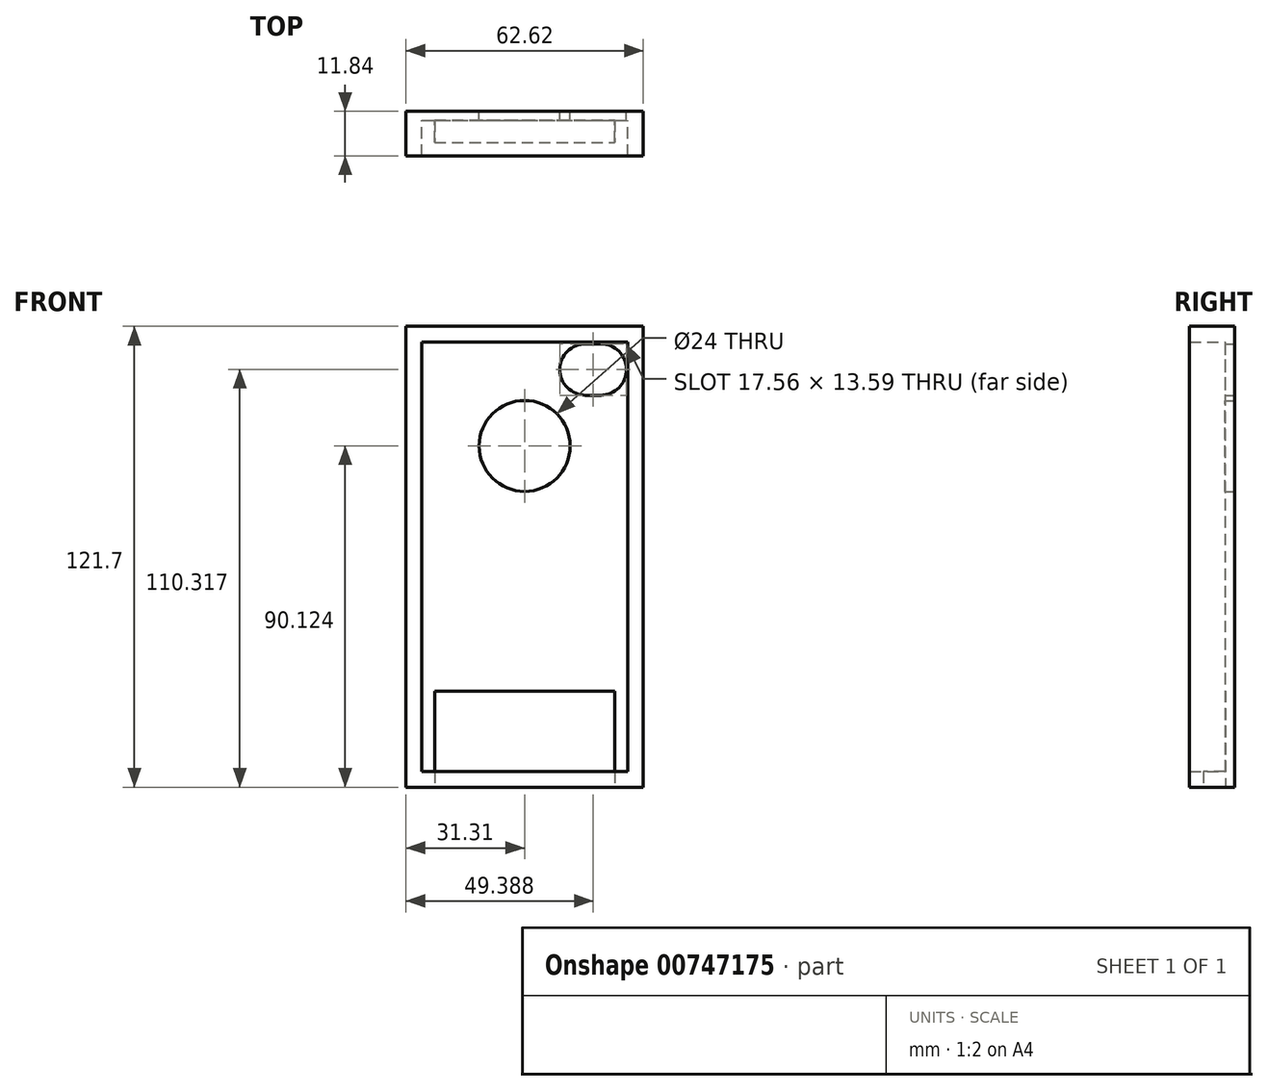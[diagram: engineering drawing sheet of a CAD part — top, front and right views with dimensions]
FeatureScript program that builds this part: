
annotation { "Feature Type Name" : "Feature", "Feature Type Description" : "" }
export const myFeature = defineFeature(function(context is Context, id is Id, definition is map)
    precondition{}
    {
        {
            var Q0;
            Q0=qCreatedBy(makeId("Front.planeOp"),FACE);
            var sketch = newSketch(context, id + "F0", { "sketchPlane" : qUnion([Q0])});
            skLineSegment(sketch, "E0.bottom", {"start": v(-31.3, 60.85) * mm, "end": v(31.3, 60.85) * mm});
            skLineSegment(sketch, "E0.top", {"start": v(-31.3, -60.85) * mm, "end": v(31.3, -60.85) * mm});
            skLineSegment(sketch, "E0.left", {"start": v(-31.3, 60.85) * mm, "end": v(-31.3, -60.85) * mm});
            skLineSegment(sketch, "E0.right", {"start": v(31.3, 60.85) * mm, "end": v(31.3, -60.85) * mm});
            skPoint(sketch, "E0.middle", {"position": v(0, 0) * mm});
            skLineSegment(sketch, "E1.0", {"start": v(-27.15, 56.7) * mm, "end": v(-27.15, -56.7) * mm});
            skLineSegment(sketch, "E1.1", {"start": v(-27.15, 56.7) * mm, "end": v(27.15, 56.7) * mm});
            skLineSegment(sketch, "E1.2", {"start": v(27.15, 56.7) * mm, "end": v(27.15, -56.7) * mm});
            skLineSegment(sketch, "E1.3", {"start": v(-27.15, -56.7) * mm, "end": v(27.15, -56.7) * mm});
            skCircle(sketch, "E2", {"center": v(0, 29.27) * mm, "radius": 12 * mm});
            skLineSegment(sketch, "E3.bottom", {"start": v(16.1, 56.26) * mm, "end": v(20.07, 56.26) * mm});
            skLineSegment(sketch, "E3.top", {"start": v(16.1, 42.67) * mm, "end": v(20.07, 42.67) * mm});
            skArc(sketch, "E4", {"start": v(16.1, 56.26) * mm, "mid": v(9.3, 49.47) * mm, "end": v(16.1, 42.67) * mm});
            skArc(sketch, "E5", {"start": v(20.07, 42.67) * mm, "mid": v(26.86, 49.47) * mm, "end": v(20.07, 56.26) * mm});
            skLineSegment(sketch, "E6", {"start": v(16.1, 49.47) * mm, "end": v(20.07, 49.47) * mm, "construction": true});
            skLineSegment(sketch, "E7", {"start": v(21.53, 49.47) * mm, "end": v(16.1, 49.47) * mm, "construction": true});
            skSolve(sketch);
        }
        {
            var Q0;
            Q0=makeQuery(id+"F0.imprint","IMPRINT",FACE,{"disambiguationData":[TD([[makeQuery(id+"F0.imprint","IMPRINT",EDGE,{"derivedFrom":sQuery(id+"F0.wireOp",EDGE,"E1.0")}),1.0]])]});
            extrude(context, id + "F1", {"entities" : qUnion([Q0]), "depth" : 2.46 * mm, "offsetDistance" : 25.4 * mm});
        }
        {
            var Q0;
            Q0 = qSketchRegion(id + "F0", true);
            extrude(context, id + "F2", {"entities" : qUnion([Q0]), "operationType" : NewBodyOperationType.ADD, "depth" : 11.84 * mm, "offsetDistance" : 25.4 * mm});
        }
        {
            var Q0;
            Q0=makeQuery(id+"F2.opExtrude","SWEPT_FACE",FACE,{"disambiguationData":[OSD([sQuery(id+"F0.wireOp",EDGE,"E0.top")])]});
            var sketch = newSketch(context, id + "F3", { "sketchPlane" : qUnion([Q0])});
            skLineSegment(sketch, "E8.bottom", {"start": v(-23.77, 8.24) * mm, "end": v(23.77, 8.24) * mm});
            skLineSegment(sketch, "E8.top", {"start": v(-23.77, 2.34) * mm, "end": v(23.77, 2.34) * mm});
            skLineSegment(sketch, "E8.left", {"start": v(-23.77, 8.24) * mm, "end": v(-23.77, 2.34) * mm});
            skLineSegment(sketch, "E8.right", {"start": v(23.77, 8.24) * mm, "end": v(23.77, 2.34) * mm});
            skSolve(sketch);
        }
        {
            var Q0;
            Q0 = qSketchRegion(id + "F3", true);
            extrude(context, id + "F4", {"entities" : qUnion([Q0]), "operationType" : NewBodyOperationType.REMOVE, "oppositeDirection" : true, "depth" : 25.4 * mm, "offsetDistance" : 25.4 * mm});
        }
    });
